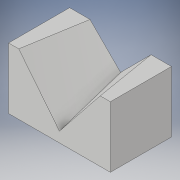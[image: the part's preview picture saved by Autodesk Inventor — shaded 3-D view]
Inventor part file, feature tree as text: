
AUTODESK INVENTOR PART (.ipt)
format: ipt  version: 2017 (Build 210142000, 142)  size: 108,032 bytes
history: native  units: in
note: dims shown in document units (in); Inventor stores cm internally (conversion verified against a paired STEP export)
features: sketch x2, extrude x1, loft x1
ambient origin geometry x8: Origin, YZ Plane, XZ Plane, XY Plane, X Axis, Y Axis, Z Axis, Center Point
bodies: Solid1 (feature_tree)
feature tree (4):
  extrude  "Extrusion1"  Depth=1.5in
  loft  "Loft1"
  sketch  "Sketch1"  dims[d0=2.5in d1=1.5in]
  sketch  "Sketch4"  dims[d2=1.5in d3=0.0in d11=0.0in d12=90.0deg d13=0.0in d14=90.0deg]
